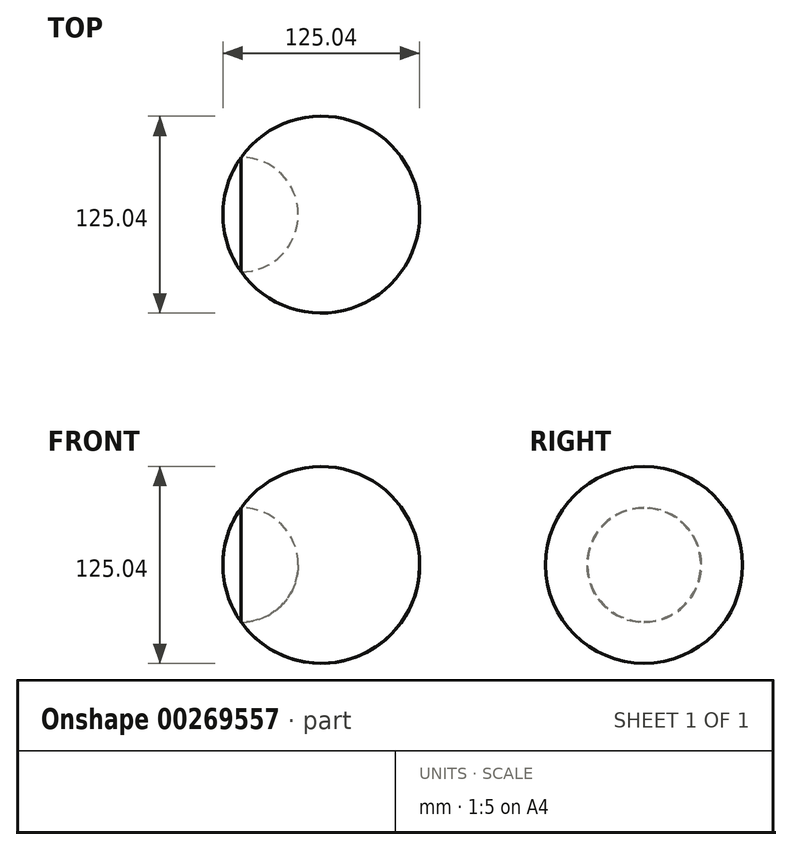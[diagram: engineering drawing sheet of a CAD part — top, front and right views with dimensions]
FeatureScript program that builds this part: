
annotation { "Feature Type Name" : "Feature", "Feature Type Description" : "" }
export const myFeature = defineFeature(function(context is Context, id is Id, definition is map)
    precondition{}
    {
        {
            var Q0;
            Q0=qCreatedBy(makeId("Front.planeOp"),FACE);
            var sketch = newSketch(context, id + "F0", { "sketchPlane" : qUnion([Q0]), "disableImprinting" : false});
            skLineSegment(sketch, "E0", {"start": v(0, 36.44) * mm, "end": v(0, -36.44) * mm});
            skLineSegment(sketch, "E1", {"start": v(0, 0) * mm, "end": v(36.44, 0) * mm});
            skArc(sketch, "E2", {"start": v(0, -36.44) * mm, "mid": v(36.44, 0) * mm, "end": v(0, 36.44) * mm});
            skSolve(sketch);
        }
        {
            var Q0;
            Q0=qCreatedBy(makeId("Front.planeOp"),FACE);
            var sketch = newSketch(context, id + "F1", { "sketchPlane" : qUnion([Q0]), "disableImprinting" : false});
            skLineSegment(sketch, "E3", {"start": v(0, 36) * mm, "end": v(0, -36) * mm});
            skArc(sketch, "E4", {"start": v(0, -36) * mm, "mid": v(113.63, 0) * mm, "end": v(0, 36) * mm});
            skLineSegment(sketch, "E5", {"start": v(0, 0) * mm, "end": v(113.63, 0) * mm});
            skArc(sketch, "E6", {"start": v(0, 36) * mm, "mid": v(-11.4, 0) * mm, "end": v(0, -36) * mm});
            skLineSegment(sketch, "E7", {"start": v(51.11, 0) * mm, "end": v(0, 36) * mm, "construction": true});
            skLineSegment(sketch, "E8", {"start": v(0, 0) * mm, "end": v(-11.4, 0) * mm});
            skLineSegment(sketch, "E9", {"start": v(0.85, 0) * mm, "end": v(0, 36) * mm, "construction": true});
            skCircle(sketch, "E10", {"center": v(0.85, 0) * mm, "radius": 36 * mm, "construction": true});
            skSolve(sketch);
        }
        {
            var Q0;
            {var subQ3=sQuery(id+"F0.wireOp",EDGE,"E1");Q0=makeQuery(id+"F0.imprint","IMPRINT",FACE,{"disambiguationData":[TD([[makeQuery(id+"F0.imprint","IMPRINT",EDGE,{"derivedFrom":subQ3}),1.0]])]});}
            var Q1;
            Q1=sQuery(id+"F0.wireOp",EDGE,"E1");
            revolve(context, id + "F2", {"surfaceOperationType" : NewSurfaceOperationType.NEW, "entities" : qUnion([Q0]), "axis" : qUnion([Q1]), "revolveType" : RevolveType.FULL});
        }
        {
            var Q0;
            {var subQ0=sQuery(id+"F1.wireOp",EDGE,"E5");Q0=makeQuery(id+"F1.imprint","IMPRINT",FACE,{"disambiguationData":[TD([[makeQuery(id+"F1.imprint","IMPRINT",EDGE,{"derivedFrom":subQ0}),1.0]])]});}
            var Q1;
            Q1=sQuery(id+"F1.wireOp",EDGE,"E5");
            revolve(context, id + "F3", {"surfaceOperationType" : NewSurfaceOperationType.NEW, "entities" : qUnion([Q0]), "axis" : qUnion([Q1]), "revolveType" : RevolveType.FULL});
        }
        {
            var Q0;
            {var subQ0=sQuery(id+"F1.wireOp",EDGE,"E8");Q0=makeQuery(id+"F1.imprint","IMPRINT",FACE,{"disambiguationData":[TD([[makeQuery(id+"F1.imprint","IMPRINT",EDGE,{"derivedFrom":subQ0}),-1.0]])]});}
            var Q1;
            Q1=sQuery(id+"F1.wireOp",EDGE,"E8");
            revolve(context, id + "F4", {"surfaceOperationType" : NewSurfaceOperationType.NEW, "entities" : qUnion([Q0]), "axis" : qUnion([Q1]), "revolveType" : RevolveType.FULL});
        }
    });
